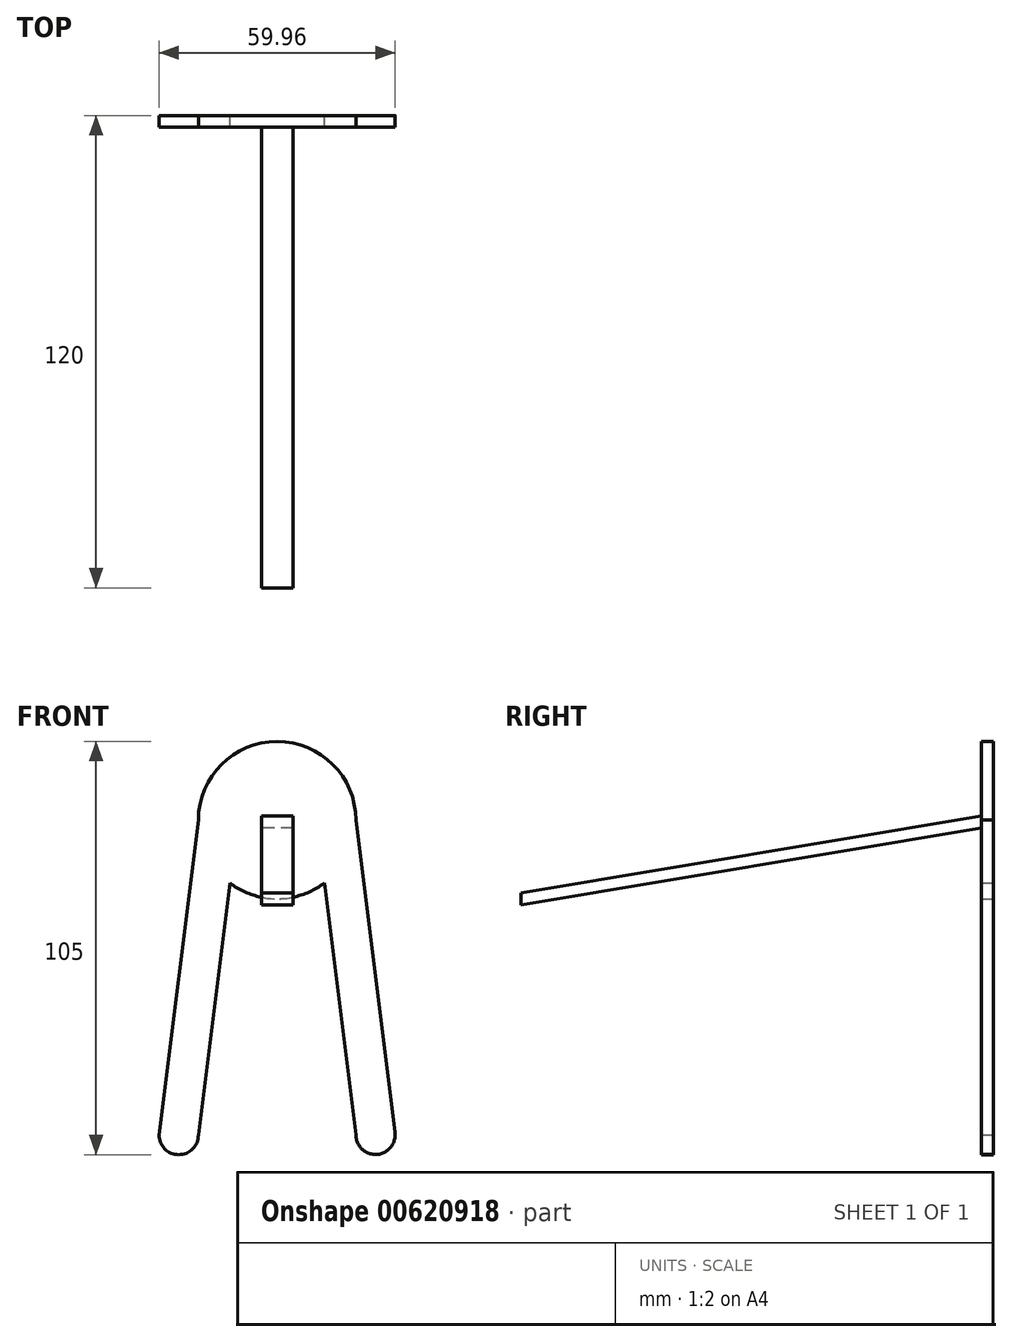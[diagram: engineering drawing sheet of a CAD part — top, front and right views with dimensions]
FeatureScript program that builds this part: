
annotation { "Feature Type Name" : "Feature", "Feature Type Description" : "" }
export const myFeature = defineFeature(function(context is Context, id is Id, definition is map)
    precondition{}
    {
        {
            var Q0;
            Q0=qCreatedBy(makeId("Front.planeOp"),FACE);
            var sketch = newSketch(context, id + "F0", { "sketchPlane" : qUnion([Q0])});
            skCircle(sketch, "E0", {"center": v(0, 0) * mm, "radius": 20 * mm});
            skLineSegment(sketch, "E1.bottom", {"start": v(-20, 0) * mm, "end": v(20, 0) * mm});
            skLineSegment(sketch, "E1.top", {"start": v(-20, -80) * mm, "end": v(20, -80) * mm});
            skLineSegment(sketch, "E1.left", {"start": v(-20, 0) * mm, "end": v(-20, -80) * mm});
            skLineSegment(sketch, "E1.right", {"start": v(20, 0) * mm, "end": v(20, -80) * mm});
            skLineSegment(sketch, "E2", {"start": v(-20, -80) * mm, "end": v(-30, -80) * mm});
            skLineSegment(sketch, "E3", {"start": v(20, -80) * mm, "end": v(30, -80) * mm});
            skLineSegment(sketch, "E4", {"start": v(20, 0) * mm, "end": v(30, -80) * mm});
            skCircle(sketch, "E5", {"center": v(0, 0) * mm, "radius": 10 * mm});
            skLineSegment(sketch, "E6", {"start": v(10, 0) * mm, "end": v(20, -80) * mm});
            skLineSegment(sketch, "E7", {"start": v(-10, 0) * mm, "end": v(-20, -80) * mm});
            skLineSegment(sketch, "E8", {"start": v(-20, 0) * mm, "end": v(-30, -80) * mm});
            skCircle(sketch, "E9", {"center": v(-25, -80) * mm, "radius": 5 * mm});
            skCircle(sketch, "E10", {"center": v(25, -80) * mm, "radius": 4.96 * mm});
            skSolve(sketch);
        }
        {
            var Q0;
            {var subQ0=sQuery(id+"F0.wireOp",EDGE,"E1.bottom");var subQ4=sQuery(id+"F0.wireOp",EDGE,"E5");var subQ6=makeQuery(id+"F0.imprint","INTERSECT",VERTEX,{"derivedFrom":[subQ0,subQ4,sQuery(id+"F0.wireOp",EDGE,"E6")]});Q0=makeQuery(id+"F0.imprint","IMPRINT",FACE,{"disambiguationData":[TD([[makeQuery(id+"F0.imprint","IMPRINT",EDGE,{"disambiguationData":[TD([[subQ6,-1.0]])],"derivedFrom":subQ4}),-1.0]])]});}
            var Q1;
            {var subQ0=sQuery(id+"F0.wireOp",EDGE,"E5");var subQ1=sQuery(id+"F0.wireOp",EDGE,"E1.bottom");var subQ2=makeQuery(id+"F0.imprint","INTERSECT",VERTEX,{"derivedFrom":[subQ1,subQ0,sQuery(id+"F0.wireOp",EDGE,"E6")]});Q1=makeQuery(id+"F0.imprint","IMPRINT",FACE,{"disambiguationData":[TD([[makeQuery(id+"F0.imprint","IMPRINT",EDGE,{"disambiguationData":[TD([[subQ2,1.0]])],"derivedFrom":subQ1}),1.0]])]});}
            var Q2;
            {var subQ0=sQuery(id+"F0.wireOp",EDGE,"E5");var subQ1=sQuery(id+"F0.wireOp",EDGE,"E1.bottom");var subQ2=makeQuery(id+"F0.imprint","INTERSECT",VERTEX,{"derivedFrom":[subQ1,subQ0,sQuery(id+"F0.wireOp",EDGE,"E6")]});Q2=makeQuery(id+"F0.imprint","IMPRINT",FACE,{"disambiguationData":[TD([[makeQuery(id+"F0.imprint","IMPRINT",EDGE,{"disambiguationData":[TD([[subQ2,1.0]])],"derivedFrom":subQ1}),-1.0]])]});}
            var Q3;
            {var subQ1=sQuery(id+"F0.wireOp",EDGE,"E0");var subQ3=sQuery(id+"F0.wireOp",EDGE,"E7");var subQ4=makeQuery(id+"F0.imprint","INTERSECT",VERTEX,{"derivedFrom":[subQ1,subQ3]});Q3=makeQuery(id+"F0.imprint","IMPRINT",FACE,{"disambiguationData":[TD([[makeQuery(id+"F0.imprint","IMPRINT",EDGE,{"disambiguationData":[TD([[subQ4,1.0]])],"derivedFrom":subQ3}),-1.0]])]});}
            var Q4;
            {var subQ0=sQuery(id+"F0.wireOp",EDGE,"E7");var subQ1=sQuery(id+"F0.wireOp",EDGE,"E0");var subQ2=makeQuery(id+"F0.imprint","INTERSECT",VERTEX,{"derivedFrom":[subQ1,subQ0]});Q4=makeQuery(id+"F0.imprint","IMPRINT",FACE,{"disambiguationData":[TD([[makeQuery(id+"F0.imprint","IMPRINT",EDGE,{"disambiguationData":[TD([[subQ2,-1.0]])],"derivedFrom":subQ1}),1.0]])]});}
            var Q5;
            {var subQ1=sQuery(id+"F0.wireOp",EDGE,"E0");var subQ3=sQuery(id+"F0.wireOp",EDGE,"E6");var subQ4=makeQuery(id+"F0.imprint","INTERSECT",VERTEX,{"derivedFrom":[subQ1,subQ3]});Q5=makeQuery(id+"F0.imprint","IMPRINT",FACE,{"disambiguationData":[TD([[makeQuery(id+"F0.imprint","IMPRINT",EDGE,{"disambiguationData":[TD([[subQ4,1.0]])],"derivedFrom":subQ3}),1.0]])]});}
            var Q6;
            {var subQ0=sQuery(id+"F0.wireOp",EDGE,"E1.right");Q6=makeQuery(id+"F0.imprint","IMPRINT",FACE,{"disambiguationData":[TD([[makeQuery(id+"F0.imprint","IMPRINT",EDGE,{"derivedFrom":subQ0}),-1.0]])]});}
            var Q7;
            {var subQ0=sQuery(id+"F0.wireOp",EDGE,"E1.right");Q7=makeQuery(id+"F0.imprint","IMPRINT",FACE,{"disambiguationData":[TD([[makeQuery(id+"F0.imprint","IMPRINT",EDGE,{"derivedFrom":subQ0}),1.0]])]});}
            var Q8;
            {var subQ0=sQuery(id+"F0.wireOp",EDGE,"E1.left");Q8=makeQuery(id+"F0.imprint","IMPRINT",FACE,{"disambiguationData":[TD([[makeQuery(id+"F0.imprint","IMPRINT",EDGE,{"derivedFrom":subQ0}),1.0]])]});}
            var Q9;
            {var subQ0=sQuery(id+"F0.wireOp",EDGE,"E1.left");Q9=makeQuery(id+"F0.imprint","IMPRINT",FACE,{"disambiguationData":[TD([[makeQuery(id+"F0.imprint","IMPRINT",EDGE,{"derivedFrom":subQ0}),-1.0]])]});}
            var Q10;
            {var subQ0=sQuery(id+"F0.wireOp",EDGE,"E2");Q10=makeQuery(id+"F0.imprint","IMPRINT",FACE,{"disambiguationData":[TD([[makeQuery(id+"F0.imprint","IMPRINT",EDGE,{"derivedFrom":subQ0}),-1.0]])]});}
            var Q11;
            {var subQ0=sQuery(id+"F0.wireOp",EDGE,"E2");Q11=makeQuery(id+"F0.imprint","IMPRINT",FACE,{"disambiguationData":[TD([[makeQuery(id+"F0.imprint","IMPRINT",EDGE,{"derivedFrom":subQ0}),1.0]])]});}
            var Q12;
            {var subQ0=sQuery(id+"F0.wireOp",EDGE,"E10");var subQ1=sQuery(id+"F0.wireOp",EDGE,"E3");var subQ2=makeQuery(id+"F0.imprint","INTERSECT",VERTEX,{"disambiguationData":[OD(0.0)],"derivedFrom":[subQ1,subQ0]});Q12=makeQuery(id+"F0.imprint","IMPRINT",FACE,{"disambiguationData":[TD([[makeQuery(id+"F0.imprint","IMPRINT",EDGE,{"disambiguationData":[TD([[subQ2,-1.0]])],"derivedFrom":subQ1}),-1.0]])]});}
            var Q13;
            {var subQ0=sQuery(id+"F0.wireOp",EDGE,"E10");var subQ1=sQuery(id+"F0.wireOp",EDGE,"E3");var subQ2=makeQuery(id+"F0.imprint","INTERSECT",VERTEX,{"disambiguationData":[OD(0.0)],"derivedFrom":[subQ1,subQ0]});Q13=makeQuery(id+"F0.imprint","IMPRINT",FACE,{"disambiguationData":[TD([[makeQuery(id+"F0.imprint","IMPRINT",EDGE,{"disambiguationData":[TD([[subQ2,-1.0]])],"derivedFrom":subQ1}),1.0]])]});}
            extrude(context, id + "F1", {"entities" : qUnion([Q0, Q1, Q2, Q3, Q4, Q5, Q6, Q7, Q8, Q9, Q10, Q11, Q12, Q13]), "depth" : 3 * mm, "offsetDistance" : 25 * mm});
        }
        {
            var Q0;
            Q0=qCreatedBy(makeId("Front.planeOp"),FACE);
            cPlane(context, id + "F2", {"entities" : qUnion([Q0]), "cplaneType" : CPlaneType.OFFSET, "offset" : 120 * mm, "width" : 150 * mm, "height" : 150 * mm});
        }
        {
            var Q0;
            Q0=qCreatedBy(id+"F2.planeOp",FACE);
            var sketch = newSketch(context, id + "F3", { "sketchPlane" : qUnion([Q0])});
            skLineSegment(sketch, "E11", {"start": v(0, 0) * mm, "end": v(0, -20) * mm});
            skLineSegment(sketch, "E12.bottom", {"start": v(-4, -18.5) * mm, "end": v(4, -18.5) * mm});
            skLineSegment(sketch, "E12.top", {"start": v(-4, -21.5) * mm, "end": v(4, -21.5) * mm});
            skLineSegment(sketch, "E12.left", {"start": v(-4, -18.5) * mm, "end": v(-4, -21.5) * mm});
            skLineSegment(sketch, "E12.right", {"start": v(4, -18.5) * mm, "end": v(4, -21.5) * mm});
            skPoint(sketch, "E12.middle", {"position": v(0, -20) * mm});
            skSolve(sketch);
        }
        {
            var Q0;
            Q0=qCreatedBy(makeId("Front.planeOp"),FACE);
            var sketch = newSketch(context, id + "F4", { "sketchPlane" : qUnion([Q0])});
            skLineSegment(sketch, "E13.bottom", {"start": v(4, 1.5) * mm, "end": v(-4, 1.5) * mm});
            skLineSegment(sketch, "E13.top", {"start": v(4, -1.5) * mm, "end": v(-4, -1.5) * mm});
            skLineSegment(sketch, "E13.left", {"start": v(4, 1.5) * mm, "end": v(4, -1.5) * mm});
            skLineSegment(sketch, "E13.right", {"start": v(-4, 1.5) * mm, "end": v(-4, -1.5) * mm});
            skPoint(sketch, "E13.middle", {"position": v(0, 0) * mm});
            skSolve(sketch);
        }
        {
            var Q1;
            Q1 = qSketchRegion(id + "F4", true);
            var Q2;
            Q2 = qSketchRegion(id + "F3", true);
            loft(context, id + "F5", {"operationType" : NewBodyOperationType.ADD, "sheetProfilesArray" : [{ "sheetProfileEntities" : qUnion([Q1]) }, { "sheetProfileEntities" : qUnion([Q2]) }]});
        }
    });
